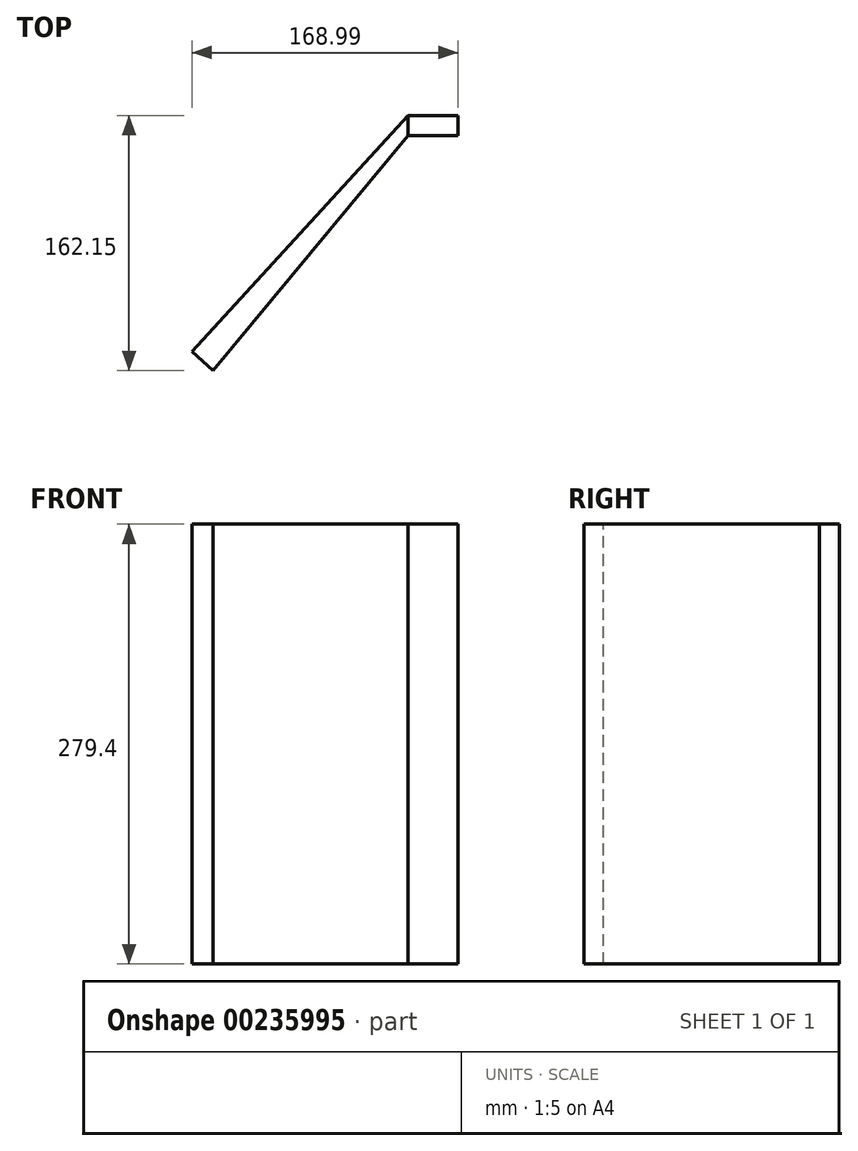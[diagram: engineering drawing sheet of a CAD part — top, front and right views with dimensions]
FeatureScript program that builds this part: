
annotation { "Feature Type Name" : "Feature", "Feature Type Description" : "" }
export const myFeature = defineFeature(function(context is Context, id is Id, definition is map)
    precondition{}
    {
        {
            var Q0;
            Q0=qCreatedBy(makeId("Front.planeOp"),FACE);
            var sketch = newSketch(context, id + "F0", { "sketchPlane" : qUnion([Q0])});
            skLineSegment(sketch, "E0.bottom", {"start": v(-15.87, 139.7) * mm, "end": v(15.88, 139.7) * mm});
            skLineSegment(sketch, "E0.top", {"start": v(-15.88, -139.7) * mm, "end": v(15.87, -139.7) * mm});
            skLineSegment(sketch, "E0.left", {"start": v(-15.87, 139.7) * mm, "end": v(-15.88, -139.7) * mm});
            skLineSegment(sketch, "E0.right", {"start": v(15.88, 139.7) * mm, "end": v(15.87, -139.7) * mm});
            skPoint(sketch, "E0.middle", {"position": v(0, 0) * mm});
            skSolve(sketch);
        }
        {
            var Q0;
            Q0=makeQuery(id+"F0.imprint","IMPRINT",FACE,{"disambiguationData":[TD([[makeQuery(id+"F0.imprint","IMPRINT",EDGE,{"derivedFrom":sQuery(id+"F0.wireOp",EDGE,"E0.bottom")}),-1.0]])]});
            extrude(context, id + "F1", {"entities" : qUnion([Q0]), "depth" : 12.7 * mm});
        }
        {
            var Q0;
            Q0=makeQuery(id+"F1.opExtrude","SWEPT_FACE",FACE,{"disambiguationData":[OSD([sQuery(id+"F0.wireOp",EDGE,"E0.bottom")])]});
            var sketch = newSketch(context, id + "F2", { "sketchPlane" : qUnion([Q0])});
            skLineSegment(sketch, "E1", {"start": v(-15.87, 0) * mm, "end": v(-153.11, -149.85) * mm});
            skLineSegment(sketch, "E2", {"start": v(-153.11, -149.85) * mm, "end": v(-139.69, -162.15) * mm});
            skLineSegment(sketch, "E3", {"start": v(-139.69, -162.15) * mm, "end": v(-15.88, -12.7) * mm});
            skLineSegment(sketch, "E4", {"start": v(-15.87, -12.7) * mm, "end": v(-15.87, 0) * mm});
            skSolve(sketch);
        }
        {
            var Q0;
            Q0=makeQuery(id+"F2.imprint","IMPRINT",FACE,{"disambiguationData":[TD([[makeQuery(id+"F2.imprint","IMPRINT",EDGE,{"derivedFrom":sQuery(id+"F2.wireOp",EDGE,"E1")}),1.0]])]});
            extrude(context, id + "F3", {"entities" : qUnion([Q0]), "oppositeDirection" : true, "depth" : 279.4 * mm});
        }
    });
